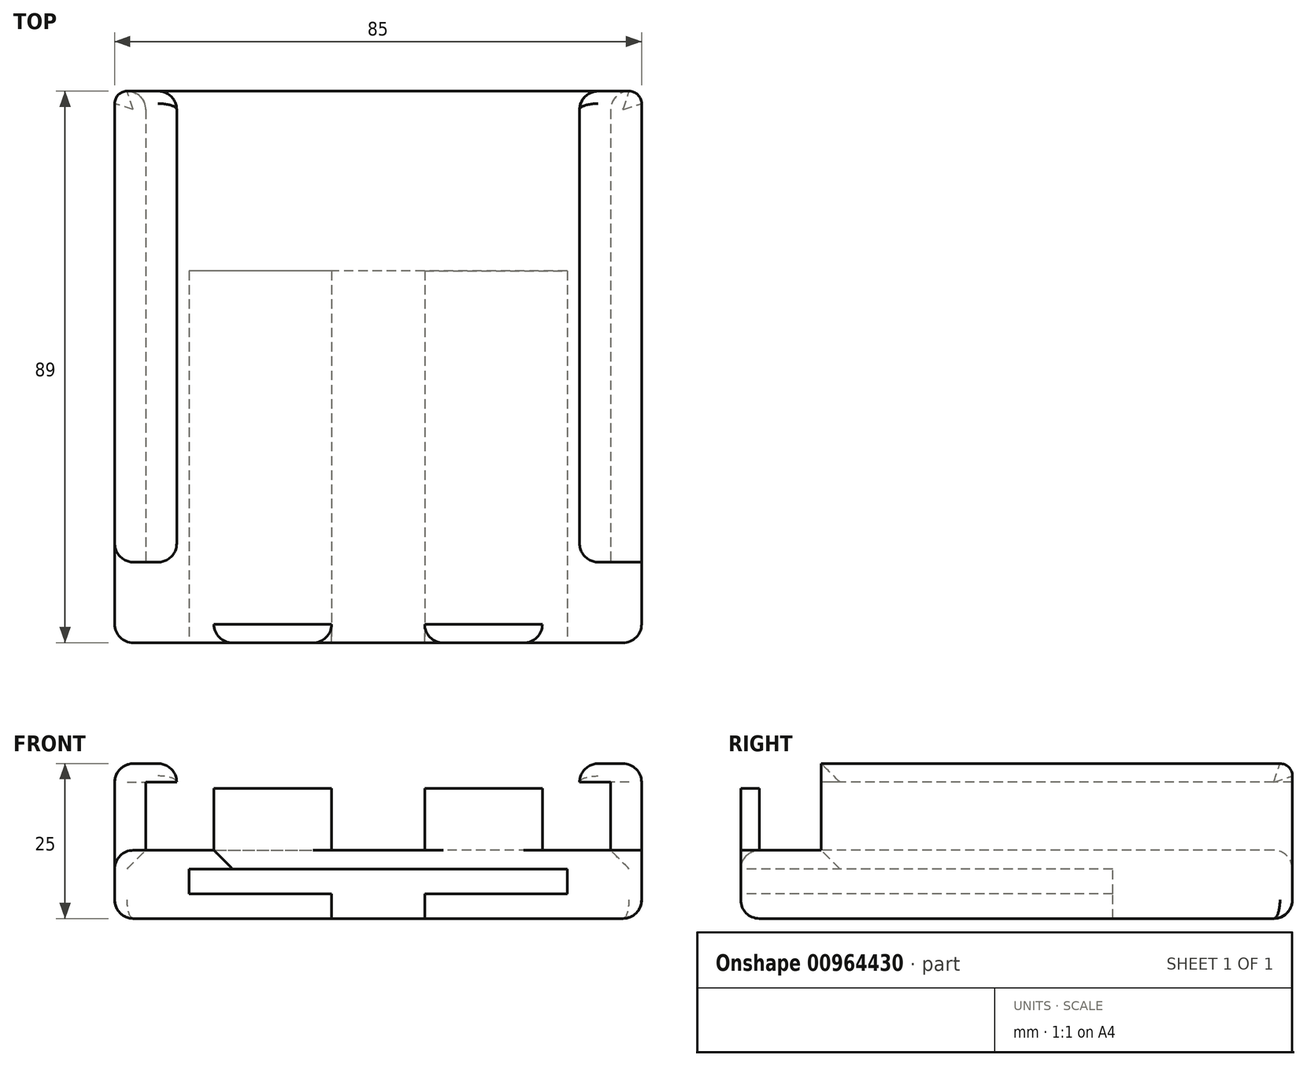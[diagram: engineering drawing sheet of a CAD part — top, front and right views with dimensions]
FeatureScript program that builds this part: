
annotation { "Feature Type Name" : "Feature", "Feature Type Description" : "" }
export const myFeature = defineFeature(function(context is Context, id is Id, definition is map)
    precondition{}
    {
        {
            var Q0;
            Q0=qCreatedBy(makeId("Front.planeOp"),FACE);
            var sketch = newSketch(context, id + "F0", { "sketchPlane" : qUnion([Q0])});
            skLineSegment(sketch, "E0.top", {"start": v(-37.5, 11) * mm, "end": v(37.5, 11) * mm});
            skLineSegment(sketch, "E0.left", {"start": v(-42.5, 0) * mm, "end": v(-42.5, 11) * mm});
            skLineSegment(sketch, "E1.left", {"start": v(-42.5, 11) * mm, "end": v(-42.5, 22) * mm});
            skLineSegment(sketch, "E1.right", {"start": v(-37.5, 11) * mm, "end": v(-37.5, 22) * mm});
            skLineSegment(sketch, "E2.MirrorCS", {"start": v(37.5, 11) * mm, "end": v(37.5, 22) * mm});
            skLineSegment(sketch, "E3.MirrorCS", {"start": v(42.5, 11) * mm, "end": v(42.5, 22) * mm});
            skLineSegment(sketch, "E4.bottom", {"start": v(-37.5, 22) * mm, "end": v(-32.5, 22) * mm});
            skLineSegment(sketch, "E4.top", {"start": v(-42.5, 25) * mm, "end": v(-32.5, 25) * mm});
            skLineSegment(sketch, "E4.left", {"start": v(-42.5, 22) * mm, "end": v(-42.5, 25) * mm});
            skLineSegment(sketch, "E4.right", {"start": v(-32.5, 22) * mm, "end": v(-32.5, 25) * mm});
            skLineSegment(sketch, "E5.MirrorCS", {"start": v(32.5, 22) * mm, "end": v(32.5, 25) * mm});
            skLineSegment(sketch, "E6.MirrorCS", {"start": v(37.5, 22) * mm, "end": v(32.5, 22) * mm});
            skLineSegment(sketch, "E7.MirrorCS", {"start": v(42.5, 25) * mm, "end": v(32.5, 25) * mm});
            skLineSegment(sketch, "E8.MirrorCS", {"start": v(42.5, 22) * mm, "end": v(42.5, 25) * mm});
            skPoint(sketch, "E9.orphan", {"position": v(42.5, 22) * mm});
            skLineSegment(sketch, "E10", {"start": v(0, 0) * mm, "end": v(-42.5, 0) * mm});
            skLineSegment(sketch, "E11.MirrorCS", {"start": v(0, 0) * mm, "end": v(42.5, 0) * mm});
            skLineSegment(sketch, "E12", {"start": v(42.5, 0) * mm, "end": v(42.5, 11) * mm});
            skSolve(sketch);
        }
        {
            var Q0;
            Q0 = qSketchRegion(id + "F0", true);
            extrude(context, id + "F1", {"entities" : qUnion([Q0]), "oppositeDirection" : true, "depth" : 89 * mm, "offsetDistance" : 25 * mm});
        }
        {
            var Q0;
            Q0=makeQuery(id+"F1.opExtrude","CAP_FACE",FACE,{"disambiguationData":[OSD([sQuery(id+"F0.wireOp",EDGE,"E0.bottom"),sQuery(id+"F0.wireOp",EDGE,"E0.top"),sQuery(id+"F0.wireOp",EDGE,"E0.left"),sQuery(id+"F0.wireOp",EDGE,"E0.right"),sQuery(id+"F0.wireOp",EDGE,"E1.left"),sQuery(id+"F0.wireOp",EDGE,"E1.right"),sQuery(id+"F0.wireOp",EDGE,"E2.MirrorCS"),sQuery(id+"F0.wireOp",EDGE,"E3.MirrorCS"),sQuery(id+"F0.wireOp",EDGE,"E4.bottom"),sQuery(id+"F0.wireOp",EDGE,"E4.top"),sQuery(id+"F0.wireOp",EDGE,"E4.left"),sQuery(id+"F0.wireOp",EDGE,"E4.right"),sQuery(id+"F0.wireOp",EDGE,"E5.MirrorCS"),sQuery(id+"F0.wireOp",EDGE,"E6.MirrorCS"),sQuery(id+"F0.wireOp",EDGE,"E7.MirrorCS"),sQuery(id+"F0.wireOp",EDGE,"E8.MirrorCS"),sQuery(id+"F0.wireOp",EDGE,"76090a21-6cb4-4435-8f2e-8d4274bf0c5a.trimOffspring"),sQuery(id+"F0.wireOp",EDGE,"RIpLdX9Q-YnJb-8AaG-gu5X-Bq0xLGxB3of3")])],"isStart":true});
            var sketch = newSketch(context, id + "F2", { "sketchPlane" : qUnion([Q0])});
            skLineSegment(sketch, "E13", {"start": v(-7.5, 0) * mm, "end": v(-7.5, 4) * mm});
            skLineSegment(sketch, "E14", {"start": v(-7.5, 4) * mm, "end": v(-30.5, 4) * mm});
            skLineSegment(sketch, "E15", {"start": v(-30.5, 4) * mm, "end": v(-30.5, 8) * mm});
            skLineSegment(sketch, "E16", {"start": v(-30.5, 8) * mm, "end": v(0, 8) * mm});
            skLineSegment(sketch, "E17.MirrorCS", {"start": v(30.5, 8) * mm, "end": v(0, 8) * mm});
            skLineSegment(sketch, "E18.MirrorCS", {"start": v(30.5, 4) * mm, "end": v(30.5, 8) * mm});
            skLineSegment(sketch, "E19.MirrorCS", {"start": v(7.5, 4) * mm, "end": v(30.5, 4) * mm});
            skLineSegment(sketch, "E20.MirrorCS", {"start": v(7.5, 0) * mm, "end": v(7.5, 4) * mm});
            skLineSegment(sketch, "E21", {"start": v(-7.5, 0) * mm, "end": v(7.5, 0) * mm});
            skSolve(sketch);
        }
        {
            var Q0;
            Q0 = qSketchRegion(id + "F2", true);
            extrude(context, id + "F3", {"entities" : qUnion([Q0]), "operationType" : NewBodyOperationType.REMOVE, "oppositeDirection" : true, "depth" : 60 * mm, "offsetDistance" : 25 * mm});
        }
        {
            var Q0;
            Q0=makeQuery(id+"F1.opExtrude","SWEPT_FACE",FACE,{"disambiguationData":[OSD([sQuery(id+"F0.wireOp",EDGE,"E0.right"),sQuery(id+"F0.wireOp",EDGE,"E3.MirrorCS"),sQuery(id+"F0.wireOp",EDGE,"E8.MirrorCS")])]});
            var sketch = newSketch(context, id + "F4", { "sketchPlane" : qUnion([Q0])});
            skLineSegment(sketch, "E22.bottom", {"start": v(0, 25) * mm, "end": v(13, 25) * mm});
            skLineSegment(sketch, "E22.top", {"start": v(0, 11) * mm, "end": v(13, 11) * mm});
            skLineSegment(sketch, "E22.left", {"start": v(0, 25) * mm, "end": v(0, 11) * mm});
            skLineSegment(sketch, "E22.right", {"start": v(13, 25) * mm, "end": v(13, 11) * mm});
            skSolve(sketch);
        }
        {
            var Q0;
            Q0=makeQuery(id+"F4.imprint","IMPRINT",FACE,{"disambiguationData":[TD([[makeQuery(id+"F4.imprint","IMPRINT",EDGE,{"derivedFrom":sQuery(id+"F4.wireOp",EDGE,"E22.bottom")}),1.0]])]});
            extrude(context, id + "F5", {"entities" : qUnion([Q0]), "operationType" : NewBodyOperationType.REMOVE, "endBound" : BoundingType.THROUGH_ALL, "oppositeDirection" : true, "depth" : 25 * mm, "offsetDistance" : 25 * mm});
        }
        {
            var Q0;
            Q0=makeQuery(id+"F5.boolean.opBoolean","MERGE",FACE,{"derivedFrom":[makeQuery(id+"F1.opExtrude","SWEPT_FACE",FACE,{"disambiguationData":[OSD([sQuery(id+"F0.wireOp",EDGE,"E0.top")])]})],"fromTools":[makeQuery(id+"F5.opExtrude","SWEPT_FACE",FACE,{"disambiguationData":[OSD([sQuery(id+"F4.wireOp",EDGE,"E22.top")])]})]});
            var sketch = newSketch(context, id + "F6", { "sketchPlane" : qUnion([Q0])});
            skLineSegment(sketch, "E23", {"start": v(-26.5, 0) * mm, "end": v(-26.5, 3) * mm});
            skLineSegment(sketch, "E24", {"start": v(-26.5, 3) * mm, "end": v(-7.5, 3) * mm});
            skLineSegment(sketch, "E25", {"start": v(-7.5, 3) * mm, "end": v(-7.5, 0) * mm});
            skLineSegment(sketch, "E26.MirrorCS", {"start": v(7.5, 3) * mm, "end": v(7.5, 0) * mm});
            skLineSegment(sketch, "E27.MirrorCS", {"start": v(26.5, 3) * mm, "end": v(7.5, 3) * mm});
            skLineSegment(sketch, "E28.MirrorCS", {"start": v(26.5, 0) * mm, "end": v(26.5, 3) * mm});
            skSolve(sketch);
        }
        {
            var Q0;
            {var subQ1=sQuery(id+"F6.wireOp",EDGE,"E23");Q0=makeQuery(id+"F6.imprint","IMPRINT",FACE,{"disambiguationData":[TD([[makeQuery(id+"F6.imprint","IMPRINT",EDGE,{"derivedFrom":subQ1}),-1.0]])]});}
            var Q1;
            {var subQ0=sQuery(id+"F6.wireOp",EDGE,"E26.MirrorCS");Q1=makeQuery(id+"F6.imprint","IMPRINT",FACE,{"disambiguationData":[TD([[makeQuery(id+"F6.imprint","IMPRINT",EDGE,{"derivedFrom":subQ0}),1.0]])]});}
            extrude(context, id + "F7", {"entities" : qUnion([Q0, Q1]), "operationType" : NewBodyOperationType.ADD, "depth" : 10 * mm, "offsetDistance" : 25 * mm});
        }
        {
            var Q0;
            Q0=makeQuery(id+"F5.boolean.opBoolean","COPY",EDGE,{"derivedFrom":makeQuery(id+"F5.opExtrude","CAP_EDGE",EDGE,{"disambiguationData":[OSD([sQuery(id+"F4.wireOp",EDGE,"E22.right")])],"isStart":true})});
            var Q1;
            Q1=makeQuery(id+"F1.opExtrude","SWEPT_EDGE",EDGE,{"disambiguationData":[OSD([sQuery(id+"F0.wireOp",EDGE,"E7.MirrorCS"),sQuery(id+"F0.wireOp",EDGE,"E8.MirrorCS")])]});
            var Q2;
            {var subQ0=sQuery(id+"F0.wireOp",EDGE,"E7.MirrorCS");var subQ1=sQuery(id+"F4.wireOp",EDGE,"E22.right");Q2=makeQuery(id+"F5.boolean.opBoolean","COPY",EDGE,{"disambiguationData":[topologyDisambiguationEdgeConnected([makeQuery(id+"F1.opExtrude","SWEPT_FACE",FACE,{"disambiguationData":[OSD([subQ0])]})])],"derivedFrom":makeQuery(id+"F5.opExtrude","SWEPT_EDGE",EDGE,{"disambiguationData":[OSD([subQ0,sQuery(id+"F0.wireOp",EDGE,"E8.MirrorCS"),sQuery(id+"F4.wireOp",EDGE,"E22.bottom"),subQ1])]})});}
            var Q3;
            Q3=makeQuery(id+"F5.boolean.opBoolean","INTERSECT",EDGE,{"derivedFrom":[makeQuery(id+"F1.opExtrude","SWEPT_FACE",FACE,{"disambiguationData":[OSD([sQuery(id+"F0.wireOp",EDGE,"E5.MirrorCS")])]}),makeQuery(id+"F5.opExtrude","SWEPT_FACE",FACE,{"disambiguationData":[OSD([sQuery(id+"F4.wireOp",EDGE,"E22.right")])]})]});
            var Q4;
            Q4=makeQuery(id+"F1.opExtrude","SWEPT_EDGE",EDGE,{"disambiguationData":[OSD([sQuery(id+"F0.wireOp",EDGE,"E5.MirrorCS"),sQuery(id+"F0.wireOp",EDGE,"E7.MirrorCS")])]});
            var Q5;
            Q5=makeQuery(id+"F1.opExtrude","CAP_EDGE",EDGE,{"disambiguationData":[OSD([sQuery(id+"F0.wireOp",EDGE,"E5.MirrorCS")])],"isStart":false});
            fillet(context, id + "F8", {"entities" : qUnion([Q0, Q1, Q2, Q3, Q4, Q5]), "radius" : 3 * mm, "tangentPropagation" : true, "allowEdgeOverflow" : false});
        }
        {
            var Q0;
            Q0=makeQuery(id+"F5.boolean.opBoolean","INTERSECT",EDGE,{"derivedFrom":[makeQuery(id+"F1.opExtrude","SWEPT_FACE",FACE,{"disambiguationData":[OSD([sQuery(id+"F0.wireOp",EDGE,"E4.right")])]}),makeQuery(id+"F5.opExtrude","SWEPT_FACE",FACE,{"disambiguationData":[OSD([sQuery(id+"F4.wireOp",EDGE,"E22.right")])]})]});
            var Q1;
            {var subQ0=sQuery(id+"F4.wireOp",EDGE,"E22.right");Q1=makeQuery(id+"F5.boolean.opBoolean","COPY",EDGE,{"disambiguationData":[topologyDisambiguationEdgeConnected([makeQuery(id+"F1.opExtrude","SWEPT_FACE",FACE,{"disambiguationData":[OSD([sQuery(id+"F0.wireOp",EDGE,"E4.top")])]})])],"derivedFrom":makeQuery(id+"F5.opExtrude","SWEPT_EDGE",EDGE,{"disambiguationData":[OSD([sQuery(id+"F0.wireOp",EDGE,"E7.MirrorCS"),sQuery(id+"F0.wireOp",EDGE,"E8.MirrorCS"),sQuery(id+"F4.wireOp",EDGE,"E22.bottom"),subQ0])]})});}
            var Q2;
            Q2=makeQuery(id+"F5.boolean.opBoolean","INTERSECT",EDGE,{"derivedFrom":[makeQuery(id+"F1.opExtrude","SWEPT_FACE",FACE,{"disambiguationData":[OSD([sQuery(id+"F0.wireOp",EDGE,"E0.left"),sQuery(id+"F0.wireOp",EDGE,"E1.left"),sQuery(id+"F0.wireOp",EDGE,"E4.left")])]}),makeQuery(id+"F5.opExtrude","SWEPT_FACE",FACE,{"disambiguationData":[OSD([sQuery(id+"F4.wireOp",EDGE,"E22.right")])]})]});
            var Q3;
            Q3=makeQuery(id+"F1.opExtrude","SWEPT_EDGE",EDGE,{"disambiguationData":[OSD([sQuery(id+"F0.wireOp",EDGE,"E4.top"),sQuery(id+"F0.wireOp",EDGE,"E4.right")])]});
            var Q4;
            Q4=makeQuery(id+"F1.opExtrude","SWEPT_EDGE",EDGE,{"disambiguationData":[OSD([sQuery(id+"F0.wireOp",EDGE,"E4.top"),sQuery(id+"F0.wireOp",EDGE,"E4.left")])]});
            var Q5;
            Q5=makeQuery(id+"F1.opExtrude","CAP_EDGE",EDGE,{"disambiguationData":[OSD([sQuery(id+"F0.wireOp",EDGE,"E4.right")])],"isStart":false});
            fillet(context, id + "F9", {"entities" : qUnion([Q0, Q1, Q2, Q3, Q4, Q5]), "radius" : 3 * mm, "tangentPropagation" : true, "allowEdgeOverflow" : false});
        }
        {
            var Q0;
            {var subQ0=sQuery(id+"F4.wireOp",EDGE,"E22.left");var subQ1=sQuery(id+"F4.wireOp",EDGE,"E22.top");var subQ2=sQuery(id+"F0.wireOp",EDGE,"E8.MirrorCS");var subQ3=sQuery(id+"F0.wireOp",EDGE,"E3.MirrorCS");var subQ4=sQuery(id+"F0.wireOp",EDGE,"E0.right");var subQ5=sQuery(id+"F0.wireOp",EDGE,"E0.top");var subQ6=makeQuery(id+"F5.boolean.opBoolean","MERGE",EDGE,{"derivedFrom":[makeQuery(id+"F1.opExtrude","CAP_EDGE",EDGE,{"disambiguationData":[OSD([subQ5])],"isStart":true})],"fromTools":[makeQuery(id+"F5.opExtrude","SWEPT_EDGE",EDGE,{"disambiguationData":[OSD([subQ4,subQ3,subQ2,subQ1,subQ0])]})]});Q0=makeQuery(id+"F7.opExtrude","CAP_EDGE",EDGE,{"disambiguationData":[OSD([subQ5,subQ4,subQ3,subQ2,subQ1,subQ0]),TDD([makeQuery(id+"F6.imprint","IMPRINT",EDGE,{"disambiguationData":[TD([[makeQuery(id+"F6.imprint","INTERSECT",VERTEX,{"derivedFrom":[subQ6,sQuery(id+"F6.wireOp",EDGE,"E26.MirrorCS")]}),-1.0]])],"derivedFrom":subQ6})])],"isStart":false});}
            var Q1;
            {var subQ0=sQuery(id+"F4.wireOp",EDGE,"E22.left");var subQ1=sQuery(id+"F4.wireOp",EDGE,"E22.top");var subQ2=sQuery(id+"F0.wireOp",EDGE,"E8.MirrorCS");var subQ3=sQuery(id+"F0.wireOp",EDGE,"E3.MirrorCS");var subQ4=sQuery(id+"F0.wireOp",EDGE,"E0.right");var subQ5=sQuery(id+"F0.wireOp",EDGE,"E0.top");var subQ6=makeQuery(id+"F5.boolean.opBoolean","MERGE",EDGE,{"derivedFrom":[makeQuery(id+"F1.opExtrude","CAP_EDGE",EDGE,{"disambiguationData":[OSD([subQ5])],"isStart":true})],"fromTools":[makeQuery(id+"F5.opExtrude","SWEPT_EDGE",EDGE,{"disambiguationData":[OSD([subQ4,subQ3,subQ2,subQ1,subQ0])]})]});Q1=makeQuery(id+"F7.opExtrude","CAP_EDGE",EDGE,{"disambiguationData":[OSD([subQ5,subQ4,subQ3,subQ2,subQ1,subQ0]),TDD([makeQuery(id+"F6.imprint","IMPRINT",EDGE,{"disambiguationData":[TD([[makeQuery(id+"F6.imprint","INTERSECT",VERTEX,{"derivedFrom":[subQ6,sQuery(id+"F6.wireOp",EDGE,"E23")]}),-1.0]])],"derivedFrom":subQ6})])],"isStart":false});}
            var Q2;
            Q2=makeQuery(id+"F7.opExtrude","SWEPT_EDGE",EDGE,{"disambiguationData":[OSD([sQuery(id+"F0.wireOp",EDGE,"E0.top"),sQuery(id+"F0.wireOp",EDGE,"E0.right"),sQuery(id+"F0.wireOp",EDGE,"E3.MirrorCS"),sQuery(id+"F0.wireOp",EDGE,"E8.MirrorCS"),sQuery(id+"F4.wireOp",EDGE,"E22.top"),sQuery(id+"F4.wireOp",EDGE,"E22.left"),sQuery(id+"F6.wireOp",EDGE,"E23")])]});
            var Q3;
            Q3=makeQuery(id+"F7.opExtrude","SWEPT_EDGE",EDGE,{"disambiguationData":[OSD([sQuery(id+"F0.wireOp",EDGE,"E0.top"),sQuery(id+"F0.wireOp",EDGE,"E0.right"),sQuery(id+"F0.wireOp",EDGE,"E3.MirrorCS"),sQuery(id+"F0.wireOp",EDGE,"E8.MirrorCS"),sQuery(id+"F4.wireOp",EDGE,"E22.top"),sQuery(id+"F4.wireOp",EDGE,"E22.left"),sQuery(id+"F6.wireOp",EDGE,"E25")])]});
            var Q4;
            Q4=makeQuery(id+"F7.opExtrude","SWEPT_EDGE",EDGE,{"disambiguationData":[OSD([sQuery(id+"F0.wireOp",EDGE,"E0.top"),sQuery(id+"F0.wireOp",EDGE,"E0.right"),sQuery(id+"F0.wireOp",EDGE,"E3.MirrorCS"),sQuery(id+"F0.wireOp",EDGE,"E8.MirrorCS"),sQuery(id+"F4.wireOp",EDGE,"E22.top"),sQuery(id+"F4.wireOp",EDGE,"E22.left"),sQuery(id+"F6.wireOp",EDGE,"E26.MirrorCS")])]});
            var Q5;
            Q5=makeQuery(id+"F7.opExtrude","SWEPT_EDGE",EDGE,{"disambiguationData":[OSD([sQuery(id+"F0.wireOp",EDGE,"E0.top"),sQuery(id+"F0.wireOp",EDGE,"E0.right"),sQuery(id+"F0.wireOp",EDGE,"E3.MirrorCS"),sQuery(id+"F0.wireOp",EDGE,"E8.MirrorCS"),sQuery(id+"F4.wireOp",EDGE,"E22.top"),sQuery(id+"F4.wireOp",EDGE,"E22.left"),sQuery(id+"F6.wireOp",EDGE,"E28.MirrorCS")])]});
            var Q6;
            {var subQ0=sQuery(id+"F6.wireOp",EDGE,"E28.MirrorCS");var subQ1=sQuery(id+"F0.wireOp",EDGE,"E0.top");var subQ2=sQuery(id+"F4.wireOp",EDGE,"E22.left");var subQ3=sQuery(id+"F4.wireOp",EDGE,"E22.top");var subQ4=sQuery(id+"F0.wireOp",EDGE,"E8.MirrorCS");var subQ5=sQuery(id+"F0.wireOp",EDGE,"E3.MirrorCS");var subQ6=sQuery(id+"F0.wireOp",EDGE,"E0.right");var subQ7=makeQuery(id+"F5.boolean.opBoolean","MERGE",EDGE,{"derivedFrom":[makeQuery(id+"F1.opExtrude","CAP_EDGE",EDGE,{"disambiguationData":[OSD([subQ1])],"isStart":true})],"fromTools":[makeQuery(id+"F5.opExtrude","SWEPT_EDGE",EDGE,{"disambiguationData":[OSD([subQ6,subQ5,subQ4,subQ3,subQ2])]})]});Q6=makeQuery(id+"F7.boolean.opBoolean","SPLIT",EDGE,{"disambiguationData":[TD([makeQuery(id+"F7.opExtrude","SWEPT_FACE",FACE,{"disambiguationData":[OSD([subQ0])]})])],"derivedFrom":subQ7});}
            var Q7;
            {var subQ0=sQuery(id+"F6.wireOp",EDGE,"E23");var subQ4=sQuery(id+"F4.wireOp",EDGE,"E22.left");var subQ5=sQuery(id+"F4.wireOp",EDGE,"E22.top");var subQ6=sQuery(id+"F0.wireOp",EDGE,"E8.MirrorCS");var subQ7=sQuery(id+"F0.wireOp",EDGE,"E3.MirrorCS");var subQ8=sQuery(id+"F0.wireOp",EDGE,"E0.right");var subQ9=sQuery(id+"F0.wireOp",EDGE,"E0.top");var subQ10=makeQuery(id+"F5.boolean.opBoolean","MERGE",EDGE,{"derivedFrom":[makeQuery(id+"F1.opExtrude","CAP_EDGE",EDGE,{"disambiguationData":[OSD([subQ9])],"isStart":true})],"fromTools":[makeQuery(id+"F5.opExtrude","SWEPT_EDGE",EDGE,{"disambiguationData":[OSD([subQ8,subQ7,subQ6,subQ5,subQ4])]})]});Q7=makeQuery(id+"F7.boolean.opBoolean","SPLIT",EDGE,{"disambiguationData":[TD([makeQuery(id+"F7.opExtrude","SWEPT_FACE",FACE,{"disambiguationData":[OSD([subQ0])]})])],"derivedFrom":subQ10});}
            var Q8;
            Q8=makeQuery(id+"F5.boolean.opBoolean","INTERSECT",EDGE,{"derivedFrom":[makeQuery(id+"F1.opExtrude","SWEPT_FACE",FACE,{"disambiguationData":[OSD([sQuery(id+"F0.wireOp",EDGE,"E0.left"),sQuery(id+"F0.wireOp",EDGE,"E1.left"),sQuery(id+"F0.wireOp",EDGE,"E4.left")])]}),makeQuery(id+"F5.opExtrude","SWEPT_FACE",FACE,{"disambiguationData":[OSD([sQuery(id+"F4.wireOp",EDGE,"E22.top")])]})]});
            var Q9;
            Q9=makeQuery(id+"F5.boolean.opBoolean","COPY",EDGE,{"derivedFrom":makeQuery(id+"F5.opExtrude","CAP_EDGE",EDGE,{"disambiguationData":[OSD([sQuery(id+"F4.wireOp",EDGE,"E22.top")])],"isStart":true})});
            var Q10;
            Q10=makeQuery(id+"F1.opExtrude","CAP_EDGE",EDGE,{"disambiguationData":[OSD([sQuery(id+"F0.wireOp",EDGE,"E0.top")])],"isStart":false});
            var Q11;
            Q11=makeQuery(id+"F1.opExtrude","CAP_EDGE",EDGE,{"disambiguationData":[OSD([sQuery(id+"F0.wireOp",EDGE,"E2.MirrorCS")])],"isStart":false});
            var Q12;
            Q12=makeQuery(id+"F1.opExtrude","CAP_EDGE",EDGE,{"disambiguationData":[OSD([sQuery(id+"F0.wireOp",EDGE,"E1.right")])],"isStart":false});
            var Q13;
            {var subQ1=sQuery(id+"F6.wireOp",EDGE,"E25");var subQ2=sQuery(id+"F0.wireOp",EDGE,"E0.top");var subQ3=sQuery(id+"F4.wireOp",EDGE,"E22.left");var subQ4=sQuery(id+"F4.wireOp",EDGE,"E22.top");var subQ5=sQuery(id+"F0.wireOp",EDGE,"E8.MirrorCS");var subQ6=sQuery(id+"F0.wireOp",EDGE,"E3.MirrorCS");var subQ7=sQuery(id+"F0.wireOp",EDGE,"E0.right");var subQ8=makeQuery(id+"F5.boolean.opBoolean","MERGE",EDGE,{"derivedFrom":[makeQuery(id+"F1.opExtrude","CAP_EDGE",EDGE,{"disambiguationData":[OSD([subQ2])],"isStart":true})],"fromTools":[makeQuery(id+"F5.opExtrude","SWEPT_EDGE",EDGE,{"disambiguationData":[OSD([subQ7,subQ6,subQ5,subQ4,subQ3])]})]});Q13=makeQuery(id+"F7.boolean.opBoolean","SPLIT",EDGE,{"disambiguationData":[TD([makeQuery(id+"F7.opExtrude","SWEPT_FACE",FACE,{"disambiguationData":[OSD([subQ1])]})])],"derivedFrom":subQ8});}
            fillet(context, id + "F10", {"entities" : qUnion([Q0, Q1, Q2, Q3, Q4, Q5, Q6, Q7, Q8, Q9, Q10, Q11, Q12, Q13]), "radius" : 3 * mm, "tangentPropagation" : true, "allowEdgeOverflow" : false});
        }
        {
            var Q0;
            Q0=makeQuery(id+"F1.opExtrude","CAP_EDGE",EDGE,{"disambiguationData":[OSD([sQuery(id+"F0.wireOp",EDGE,"E0.right"),sQuery(id+"F0.wireOp",EDGE,"E3.MirrorCS"),sQuery(id+"F0.wireOp",EDGE,"E8.MirrorCS")])],"isStart":true});
            var Q1;
            Q1=makeQuery(id+"F1.opExtrude","CAP_EDGE",EDGE,{"disambiguationData":[OSD([sQuery(id+"F0.wireOp",EDGE,"E0.bottom"),sQuery(id+"F0.wireOp",EDGE,"76090a21-6cb4-4435-8f2e-8d4274bf0c5a.trimOffspring"),sQuery(id+"F0.wireOp",EDGE,"RIpLdX9Q-YnJb-8AaG-gu5X-Bq0xLGxB3of3")])],"isStart":false});
            var Q2;
            Q2=makeQuery(id+"F1.opExtrude","SWEPT_EDGE",EDGE,{"disambiguationData":[OSD([sQuery(id+"F0.wireOp",EDGE,"E0.right"),sQuery(id+"F0.wireOp",EDGE,"76090a21-6cb4-4435-8f2e-8d4274bf0c5a.trimOffspring")])]});
            var Q3;
            Q3=makeQuery(id+"F1.opExtrude","SWEPT_EDGE",EDGE,{"disambiguationData":[OSD([sQuery(id+"F0.wireOp",EDGE,"E0.bottom"),sQuery(id+"F0.wireOp",EDGE,"E0.left")])]});
            var Q4;
            Q4=makeQuery(id+"F1.opExtrude","CAP_EDGE",EDGE,{"disambiguationData":[OSD([sQuery(id+"F0.wireOp",EDGE,"E0.left"),sQuery(id+"F0.wireOp",EDGE,"E1.left"),sQuery(id+"F0.wireOp",EDGE,"E4.left")])],"isStart":true});
            var Q5;
            Q5=makeQuery(id+"F1.opExtrude","SWEPT_EDGE",EDGE,{"disambiguationData":[OSD([sQuery(id+"F0.wireOp",EDGE,"E11.MirrorCS"),sQuery(id+"F0.wireOp",EDGE,"E12")])]});
            var Q6;
            {var subQ0=sQuery(id+"F0.wireOp",EDGE,"E11.MirrorCS");var subQ1=sQuery(id+"F0.wireOp",EDGE,"E10");Q6=makeQuery(id+"F3.boolean.opBoolean","SPLIT",EDGE,{"disambiguationData":[TD([makeQuery(id+"F3.opExtrude","SWEPT_FACE",FACE,{"disambiguationData":[OSD([sQuery(id+"F2.wireOp",EDGE,"E13")])]})])],"derivedFrom":makeQuery(id+"F1.opExtrude","CAP_EDGE",EDGE,{"disambiguationData":[OSD([subQ1,subQ0])],"isStart":true})});}
            var Q7;
            {var subQ1=sQuery(id+"F0.wireOp",EDGE,"E11.MirrorCS");var subQ2=sQuery(id+"F0.wireOp",EDGE,"E10");Q7=makeQuery(id+"F3.boolean.opBoolean","SPLIT",EDGE,{"disambiguationData":[TD([makeQuery(id+"F3.opExtrude","SWEPT_FACE",FACE,{"disambiguationData":[OSD([sQuery(id+"F2.wireOp",EDGE,"E20.MirrorCS")])]})])],"derivedFrom":makeQuery(id+"F1.opExtrude","CAP_EDGE",EDGE,{"disambiguationData":[OSD([subQ2,subQ1])],"isStart":true})});}
            var Q8;
            Q8=makeQuery(id+"F1.opExtrude","CAP_EDGE",EDGE,{"disambiguationData":[OSD([sQuery(id+"F0.wireOp",EDGE,"E10"),sQuery(id+"F0.wireOp",EDGE,"E11.MirrorCS")])],"isStart":false});
            fillet(context, id + "F11", {"entities" : qUnion([Q0, Q1, Q2, Q3, Q4, Q5, Q6, Q7, Q8]), "radius" : 3 * mm, "tangentPropagation" : true, "allowEdgeOverflow" : false});
        }
        {
            var Q0;
            Q0=makeQuery(id+"F1.opExtrude","CAP_EDGE",EDGE,{"disambiguationData":[OSD([sQuery(id+"F0.wireOp",EDGE,"E0.right"),sQuery(id+"F0.wireOp",EDGE,"E3.MirrorCS"),sQuery(id+"F0.wireOp",EDGE,"E8.MirrorCS")])],"isStart":false});
            var Q1;
            Q1=makeQuery(id+"F1.opExtrude","CAP_EDGE",EDGE,{"disambiguationData":[OSD([sQuery(id+"F0.wireOp",EDGE,"E0.left"),sQuery(id+"F0.wireOp",EDGE,"E1.left"),sQuery(id+"F0.wireOp",EDGE,"E4.left")])],"isStart":false});
            fillet(context, id + "F12", {"entities" : qUnion([Q0, Q1]), "radius" : 2 * mm, "tangentPropagation" : true, "allowEdgeOverflow" : false});
        }
    });
